# Revit family: 10625USA_new
name_source: partatom
category: Plumbing Fixtures
units: mm (PartAtom-declared; Revit-internal decimal feet)

## family parameters
Cut with Voids When Loaded = Yes
Host = Face
OmniClass Number = 23.31.17.00
OmniClass Title = Showers
Part Type = Normal
Room Calculation Point = No
Round Connector Dimension = Use Diameter
Shared = No

## types (2) — shared parameters
Connector Description = Water Inlet 3/4
Default Elevation = 48"
Description = AXOR ShowerSolutions ShowerHeaven 720/720 3jet 2.5 GPM without lighting
Diameter = 1"
Manufacturer = AXOR
Model = 10625USA
Product Guid = 9e131c33-2162-44ce-a14c-98cc2b5be51c
Product Page URL = https://www.axor-design.com
Product data url = https://bimobject.com
URL = https://www.axor-design.com
Version = 1

## per-type parameters (varying)
| type | Material |
| 801 Stainless Steel Optic | AXOR - Metal - 801 Stainless Steel Optic |
| 821 Brushed Nickel | AXOR - Metal - 821 Brushed Nickel |

## geometry (parser evidence)
native form markers: Sweep x2
no freeform markers — native parametric forms only
